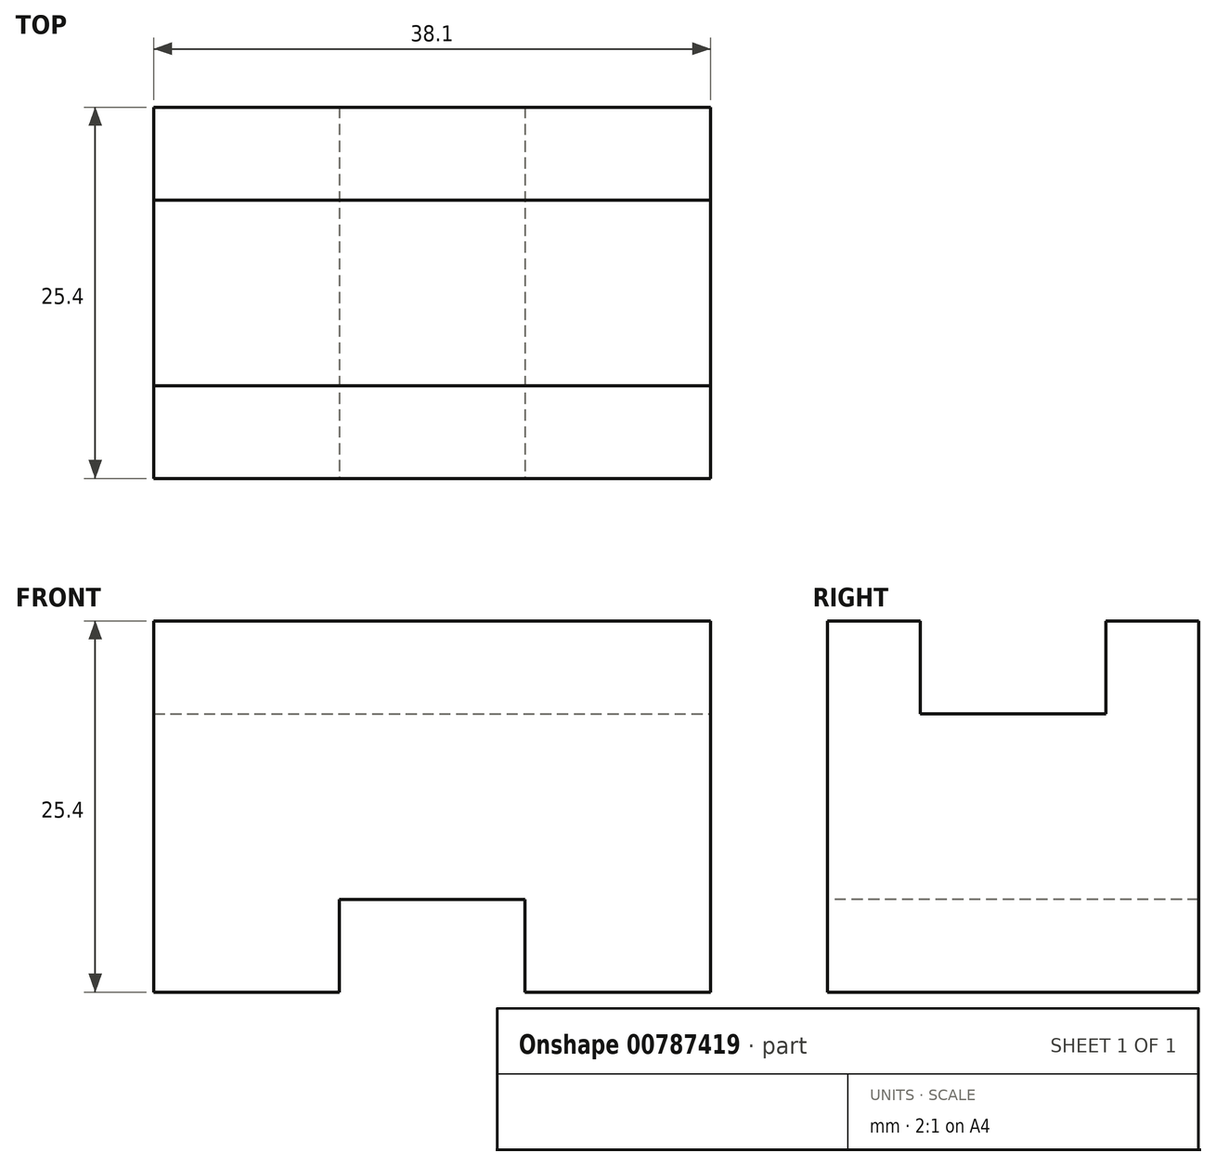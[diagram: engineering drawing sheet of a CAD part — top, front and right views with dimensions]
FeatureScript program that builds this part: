
annotation { "Feature Type Name" : "Feature", "Feature Type Description" : "" }
export const myFeature = defineFeature(function(context is Context, id is Id, definition is map)
    precondition{}
    {
        {
            var Q0;
            Q0=qCreatedBy(makeId("Front.planeOp"),FACE);
            var sketch = newSketch(context, id + "F0", { "sketchPlane" : qUnion([Q0])});
            skLineSegment(sketch, "E0", {"start": v(0, 0) * mm, "end": v(38.1, 0) * mm});
            skLineSegment(sketch, "E1", {"start": v(38.1, 0) * mm, "end": v(38.1, 25.4) * mm});
            skLineSegment(sketch, "E2", {"start": v(38.1, 25.4) * mm, "end": v(0, 25.4) * mm});
            skLineSegment(sketch, "E3", {"start": v(0, 25.4) * mm, "end": v(0, 0) * mm});
            skSolve(sketch);
        }
        {
            var Q0;
            Q0 = qSketchRegion(id + "F0", true);
            extrude(context, id + "F1", {"entities" : qUnion([Q0]), "depth" : 25.4 * mm, "offsetDistance" : 25.4 * mm});
        }
        {
            var Q0;
            Q0=makeQuery(id+"F1.opExtrude","CAP_FACE",FACE,{"disambiguationData":[OSD([sQuery(id+"F0.wireOp",EDGE,"E0"),sQuery(id+"F0.wireOp",EDGE,"E1"),sQuery(id+"F0.wireOp",EDGE,"E2"),sQuery(id+"F0.wireOp",EDGE,"E3")])],"isStart":false});
            var sketch = newSketch(context, id + "F2", { "sketchPlane" : qUnion([Q0])});
            skLineSegment(sketch, "E4", {"start": v(0, 0) * mm, "end": v(12.7, 0) * mm});
            skLineSegment(sketch, "E5", {"start": v(12.7, 0) * mm, "end": v(12.7, 6.35) * mm});
            skLineSegment(sketch, "E6", {"start": v(12.7, 6.35) * mm, "end": v(25.4, 6.35) * mm});
            skLineSegment(sketch, "E7", {"start": v(25.4, 6.35) * mm, "end": v(25.4, 0) * mm});
            skSolve(sketch);
        }
        {
            var Q0;
            Q0 = qSketchRegion(id + "F2", true);
            var Q1;
            {var subQ0=sQuery(id+"F2.wireOp",EDGE,"E5");Q1=makeQuery(id+"F2.imprint","IMPRINT",FACE,{"disambiguationData":[TD([[makeQuery(id+"F2.imprint","IMPRINT",EDGE,{"derivedFrom":subQ0}),-1.0]])]});}
            extrude(context, id + "F3", {"entities" : qUnion([Q0, Q1]), "operationType" : NewBodyOperationType.REMOVE, "oppositeDirection" : true, "depth" : 25.4 * mm, "offsetDistance" : 25.4 * mm});
        }
        {
            var Q0;
            Q0=makeQuery(id+"F1.opExtrude","SWEPT_FACE",FACE,{"disambiguationData":[OSD([sQuery(id+"F0.wireOp",EDGE,"E1")])]});
            var sketch = newSketch(context, id + "F4", { "sketchPlane" : qUnion([Q0])});
            skLineSegment(sketch, "E8", {"start": v(-25.4, 25.4) * mm, "end": v(-19.05, 25.4) * mm});
            skLineSegment(sketch, "E9", {"start": v(-19.05, 25.4) * mm, "end": v(-19.05, 19.05) * mm});
            skLineSegment(sketch, "E10", {"start": v(-19.05, 19.05) * mm, "end": v(-6.35, 19.05) * mm});
            skLineSegment(sketch, "E11", {"start": v(-6.35, 19.05) * mm, "end": v(-6.35, 25.4) * mm});
            skSolve(sketch);
        }
        {
            var Q0;
            Q0 = qSketchRegion(id + "F4", true);
            var Q1;
            {var subQ0=sQuery(id+"F4.wireOp",EDGE,"E9");Q1=makeQuery(id+"F4.imprint","IMPRINT",FACE,{"disambiguationData":[TD([[makeQuery(id+"F4.imprint","IMPRINT",EDGE,{"derivedFrom":subQ0}),1.0]])]});}
            extrude(context, id + "F5", {"entities" : qUnion([Q0, Q1]), "operationType" : NewBodyOperationType.REMOVE, "oppositeDirection" : true, "depth" : 38.1 * mm, "offsetDistance" : 25.4 * mm});
        }
    });
